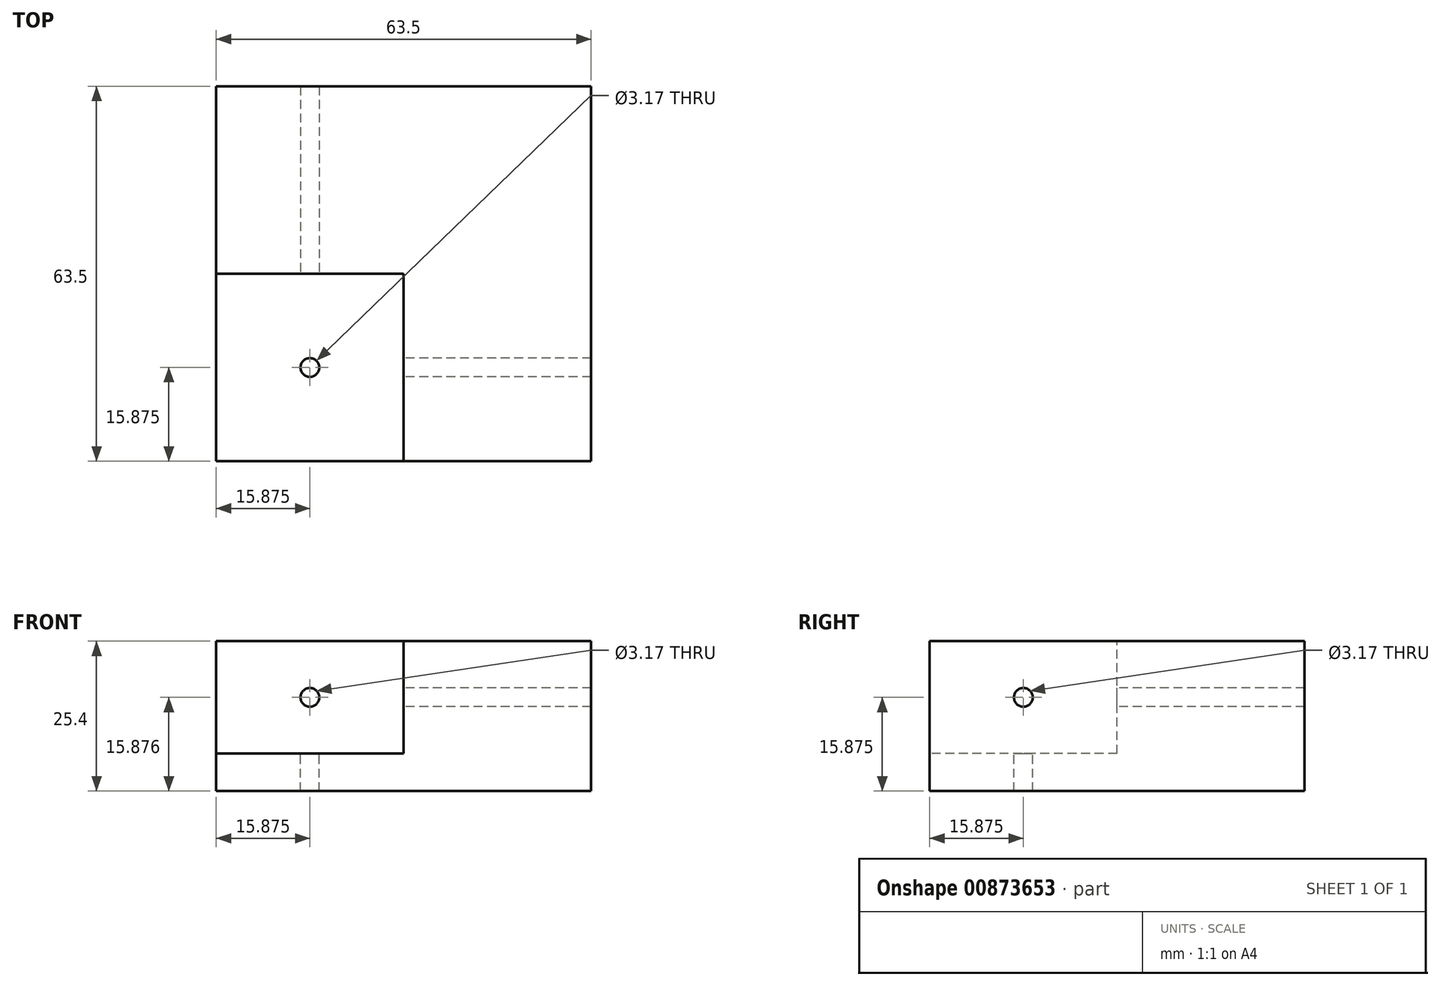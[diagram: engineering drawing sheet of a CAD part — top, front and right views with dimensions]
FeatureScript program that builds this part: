
annotation { "Feature Type Name" : "Feature", "Feature Type Description" : "" }
export const myFeature = defineFeature(function(context is Context, id is Id, definition is map)
    precondition{}
    {
        {
            var Q0;
            Q0=qCreatedBy(makeId("Top.planeOp"),FACE);
            var sketch = newSketch(context, id + "F0", { "sketchPlane" : qUnion([Q0])});
            skLineSegment(sketch, "E0.bottom", {"start": v(31.75, 31.75) * mm, "end": v(-31.75, 31.75) * mm});
            skLineSegment(sketch, "E0.top", {"start": v(31.75, -31.75) * mm, "end": v(-31.75, -31.75) * mm});
            skLineSegment(sketch, "E0.left", {"start": v(31.75, 31.75) * mm, "end": v(31.75, -31.75) * mm});
            skLineSegment(sketch, "E0.right", {"start": v(-31.75, 31.75) * mm, "end": v(-31.75, -31.75) * mm});
            skPoint(sketch, "E0.middle", {"position": v(0, 0) * mm});
            skSolve(sketch);
        }
        {
            var Q0;
            Q0 = qSketchRegion(id + "F0", true);
            extrude(context, id + "F1", {"entities" : qUnion([Q0]), "depth" : 25.4 * mm, "offsetDistance" : 25.4 * mm});
        }
        {
            var Q0;
            Q0=makeQuery(id+"F1.opExtrude","CAP_FACE",FACE,{"disambiguationData":[OSD([sQuery(id+"F0.wireOp",EDGE,"E0.bottom"),sQuery(id+"F0.wireOp",EDGE,"E0.top"),sQuery(id+"F0.wireOp",EDGE,"E0.left"),sQuery(id+"F0.wireOp",EDGE,"E0.right")])],"isStart":false});
            var sketch = newSketch(context, id + "F2", { "sketchPlane" : qUnion([Q0])});
            skLineSegment(sketch, "E1.bottom", {"start": v(-31.75, -31.75) * mm, "end": v(0, -31.75) * mm});
            skLineSegment(sketch, "E1.top", {"start": v(-31.75, 0) * mm, "end": v(0, 0) * mm});
            skLineSegment(sketch, "E1.left", {"start": v(-31.75, -31.75) * mm, "end": v(-31.75, 0) * mm});
            skLineSegment(sketch, "E1.right", {"start": v(0, -31.75) * mm, "end": v(0, 0) * mm});
            skSolve(sketch);
        }
        {
            var Q0;
            Q0 = qSketchRegion(id + "F2", true);
            var Q1;
            Q1=makeQuery(id+"F2.imprint","IMPRINT",FACE,{"disambiguationData":[TD([[makeQuery(id+"F2.imprint","IMPRINT",EDGE,{"derivedFrom":sQuery(id+"F2.wireOp",EDGE,"E1.bottom")}),-1.0]])]});
            extrude(context, id + "F3", {"entities" : qUnion([Q0, Q1]), "operationType" : NewBodyOperationType.REMOVE, "oppositeDirection" : true, "depth" : 19.05 * mm, "offsetDistance" : 25.4 * mm});
        }
        {
            var Q0;
            Q0=makeQuery(id+"F3.boolean.opBoolean","COPY",FACE,{"derivedFrom":makeQuery(id+"F3.opExtrude","CAP_FACE",FACE,{"disambiguationData":[OSD([sQuery(id+"F2.wireOp",EDGE,"E1.bottom"),sQuery(id+"F2.wireOp",EDGE,"E1.top"),sQuery(id+"F2.wireOp",EDGE,"E1.left"),sQuery(id+"F2.wireOp",EDGE,"E1.right")])],"isStart":false})});
            var sketch = newSketch(context, id + "F4", { "sketchPlane" : qUnion([Q0])});
            skCircle(sketch, "E2", {"center": v(-15.88, -15.88) * mm, "radius": 1.59 * mm});
            skSolve(sketch);
        }
        {
            var Q0;
            Q0=makeQuery(id+"F4.imprint","IMPRINT",FACE,{"disambiguationData":[TD([[makeQuery(id+"F4.imprint","IMPRINT",EDGE,{"derivedFrom":sQuery(id+"F4.wireOp",EDGE,"E2")}),1.0]])]});
            extrude(context, id + "F5", {"entities" : qUnion([Q0]), "operationType" : NewBodyOperationType.REMOVE, "oppositeDirection" : true, "depth" : 6.35 * mm, "offsetDistance" : 25.4 * mm});
        }
        {
            var Q0;
            Q0=makeQuery(id+"F3.boolean.opBoolean","COPY",FACE,{"derivedFrom":makeQuery(id+"F3.opExtrude","SWEPT_FACE",FACE,{"disambiguationData":[OSD([sQuery(id+"F2.wireOp",EDGE,"E1.right")])]})});
            var sketch = newSketch(context, id + "F6", { "sketchPlane" : qUnion([Q0])});
            skCircle(sketch, "E3", {"center": v(15.88, 15.88) * mm, "radius": 1.59 * mm});
            skSolve(sketch);
        }
        {
            var Q0;
            Q0 = qSketchRegion(id + "F6", true);
            extrude(context, id + "F7", {"entities" : qUnion([Q0]), "operationType" : NewBodyOperationType.REMOVE, "oppositeDirection" : true, "depth" : 38.1 * mm, "offsetDistance" : 25.4 * mm});
        }
        {
            var Q0;
            Q0=makeQuery(id+"F3.boolean.opBoolean","COPY",FACE,{"derivedFrom":makeQuery(id+"F3.opExtrude","SWEPT_FACE",FACE,{"disambiguationData":[OSD([sQuery(id+"F2.wireOp",EDGE,"E1.top")])]})});
            var sketch = newSketch(context, id + "F8", { "sketchPlane" : qUnion([Q0])});
            skCircle(sketch, "E4", {"center": v(-15.88, 15.88) * mm, "radius": 1.59 * mm});
            skSolve(sketch);
        }
        {
            var Q0;
            Q0 = qSketchRegion(id + "F8", true);
            extrude(context, id + "F9", {"entities" : qUnion([Q0]), "operationType" : NewBodyOperationType.REMOVE, "oppositeDirection" : true, "depth" : 38.1 * mm, "offsetDistance" : 25.4 * mm});
        }
    });
